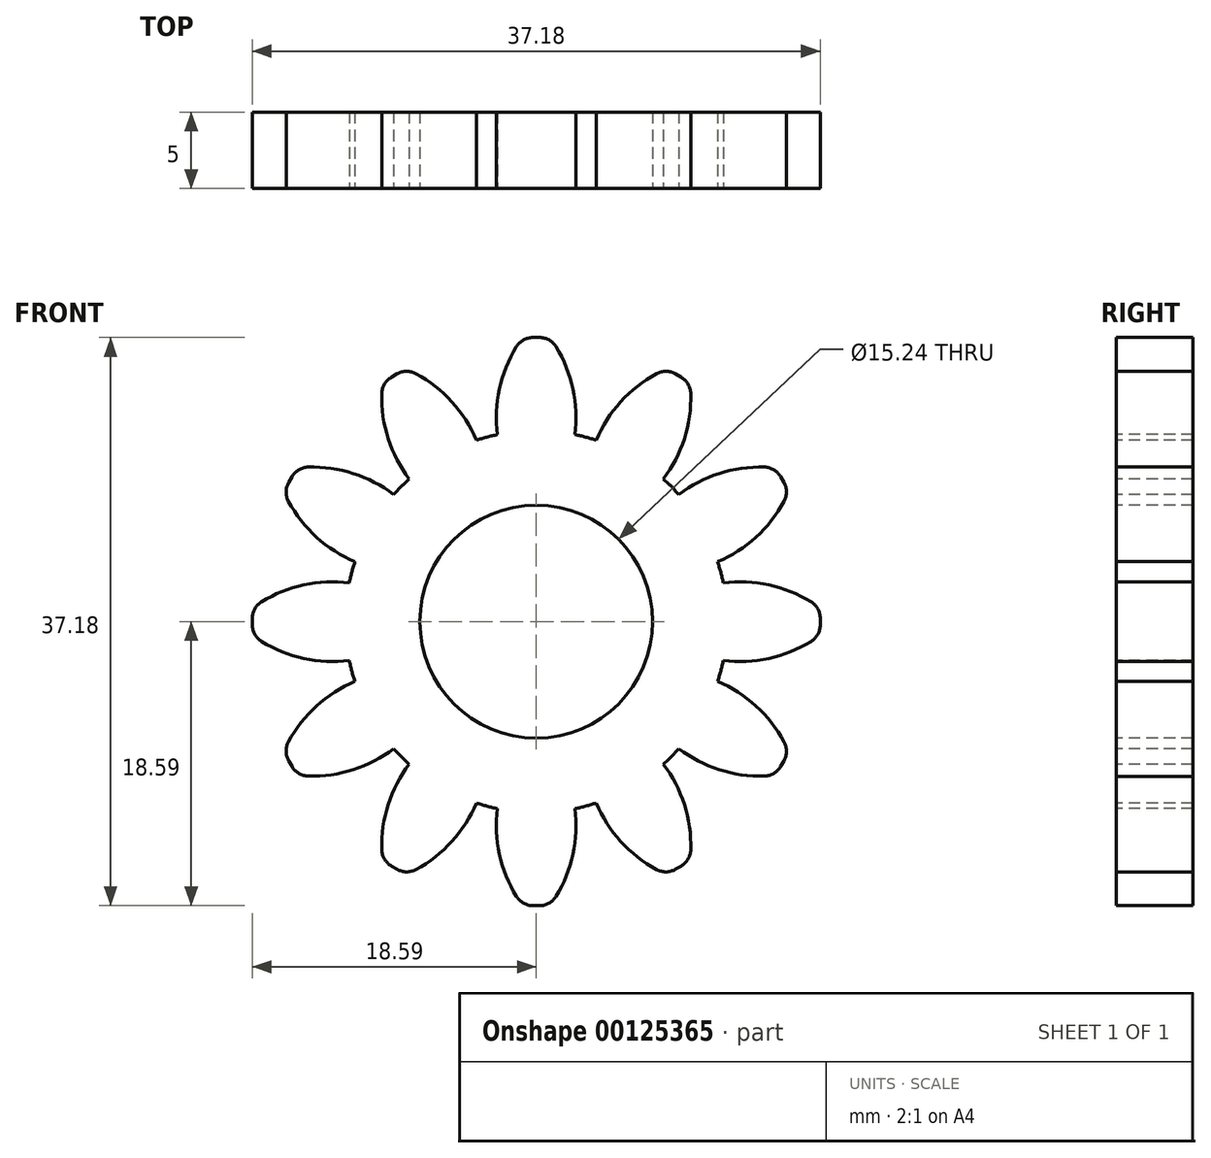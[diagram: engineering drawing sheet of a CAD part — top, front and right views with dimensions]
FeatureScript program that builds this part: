
annotation { "Feature Type Name" : "Feature", "Feature Type Description" : "" }
export const myFeature = defineFeature(function(context is Context, id is Id, definition is map)
    precondition{}
    {
        {
            var Q0;
            Q0=qCreatedBy(makeId("Front.planeOp"),FACE);
            var sketch = newSketch(context, id + "F0", { "sketchPlane" : qUnion([Q0])});
            skCircle(sketch, "E0", {"center": v(0, 0) * mm, "radius": 12.5 * mm});
            skSolve(sketch);
        }
        {
            var Q0;
            Q0 = qSketchRegion(id + "F0", true);
            extrude(context, id + "F1", {"entities" : qUnion([Q0]), "depth" : 5 * mm});
        }
        {
            var Q0;
            Q0=makeQuery(id+"F1.opExtrude","CAP_FACE",FACE,{"disambiguationData":[OSD([sQuery(id+"F0.wireOp",EDGE,"E0")])],"isStart":false});
            var sketch = newSketch(context, id + "F2", { "sketchPlane" : qUnion([Q0])});
            skArc(sketch, "E1.0", {"start": v(2.54, 12.24) * mm, "mid": v(0, 12.5) * mm, "end": v(-2.54, 12.24) * mm});
            skArc(sketch, "E2", {"start": v(-0.89, 18.59) * mm, "mid": v(-2.32, 15.57) * mm, "end": v(-2.54, 12.24) * mm});
            skArc(sketch, "E3", {"start": v(2.54, 12.24) * mm, "mid": v(2.32, 15.57) * mm, "end": v(0.89, 18.59) * mm});
            skLineSegment(sketch, "E4", {"start": v(-0.89, 18.59) * mm, "end": v(0.89, 18.59) * mm});
            skLineSegment(sketch, "E5", {"start": v(0, 18.59) * mm, "end": v(0, 0) * mm, "construction": true});
            skLineSegment(sketch, "E6", {"start": v(-2.54, 12.24) * mm, "end": v(2.54, 12.24) * mm, "construction": true});
            skSolve(sketch);
        }
        {
            var Q0;
            Q0 = qSketchRegion(id + "F2", true);
            var Q1;
            Q1=makeQuery(id+"F1.opExtrude","CAP_FACE",FACE,{"disambiguationData":[OSD([sQuery(id+"F0.wireOp",EDGE,"E0")])],"isStart":true});
            extrude(context, id + "F3", {"entities" : qUnion([Q0]), "operationType" : NewBodyOperationType.ADD, "endBound" : BoundingType.UP_TO_SURFACE, "oppositeDirection" : true, "endBoundEntityFace" : qUnion([Q1]), "depth" : 25.4 * mm});
        }
        {
            var Q0;
            Q0=makeQuery(id+"F3.opExtrude","SWEPT_EDGE",EDGE,{"disambiguationData":[OSD([sQuery(id+"F2.wireOp",EDGE,"E2"),sQuery(id+"F2.wireOp",EDGE,"E4")])]});
            var Q1;
            Q1=makeQuery(id+"F3.opExtrude","SWEPT_EDGE",EDGE,{"disambiguationData":[OSD([sQuery(id+"F2.wireOp",EDGE,"E3"),sQuery(id+"F2.wireOp",EDGE,"E4")])]});
            fillet(context, id + "F4", {"entities" : qUnion([Q0, Q1]), "radius" : 1.27 * mm, "tangentPropagation" : true, "allowEdgeOverflow" : false});
        }
        {
            var Q0;
            Q0=makeQuery(id+"F1.opExtrude","SWEPT_BODY",BODY,{"disambiguationData":[OSD([sQuery(id+"F0.wireOp",EDGE,"E0")])]});
            var Q1;
            Q1=makeQuery(id+"F1.opExtrude","SWEPT_FACE",FACE,{"disambiguationData":[OSD([sQuery(id+"F0.wireOp",EDGE,"E0")])]});
            circularPattern(context, id + "F5", {"operationType" : NewBodyOperationType.ADD, "entities" : qUnion([Q0]), "axis" : qUnion([Q1]), "angle" : 360 * degree, "instanceCount" : 12, "equalSpace" : true});
        }
        {
            var Q0;
            {var subQ0=sQuery(id+"F2.wireOp",EDGE,"E1.0");Q0=makeQuery(id+"F2.imprint","IMPRINT",FACE,{"disambiguationData":[TD([[makeQuery(id+"F2.imprint","IMPRINT",EDGE,{"derivedFrom":subQ0}),1.0]])]});}
            var sketch = newSketch(context, id + "F6", { "sketchPlane" : qUnion([Q0])});
            skCircle(sketch, "E7", {"center": v(0, 0) * mm, "radius": 7.62 * mm});
            skSolve(sketch);
        }
        {
            var Q0;
            Q0 = qSketchRegion(id + "F6", true);
            extrude(context, id + "F7", {"entities" : qUnion([Q0]), "operationType" : NewBodyOperationType.REMOVE, "oppositeDirection" : true, "depth" : 25.4 * mm});
        }
    });
